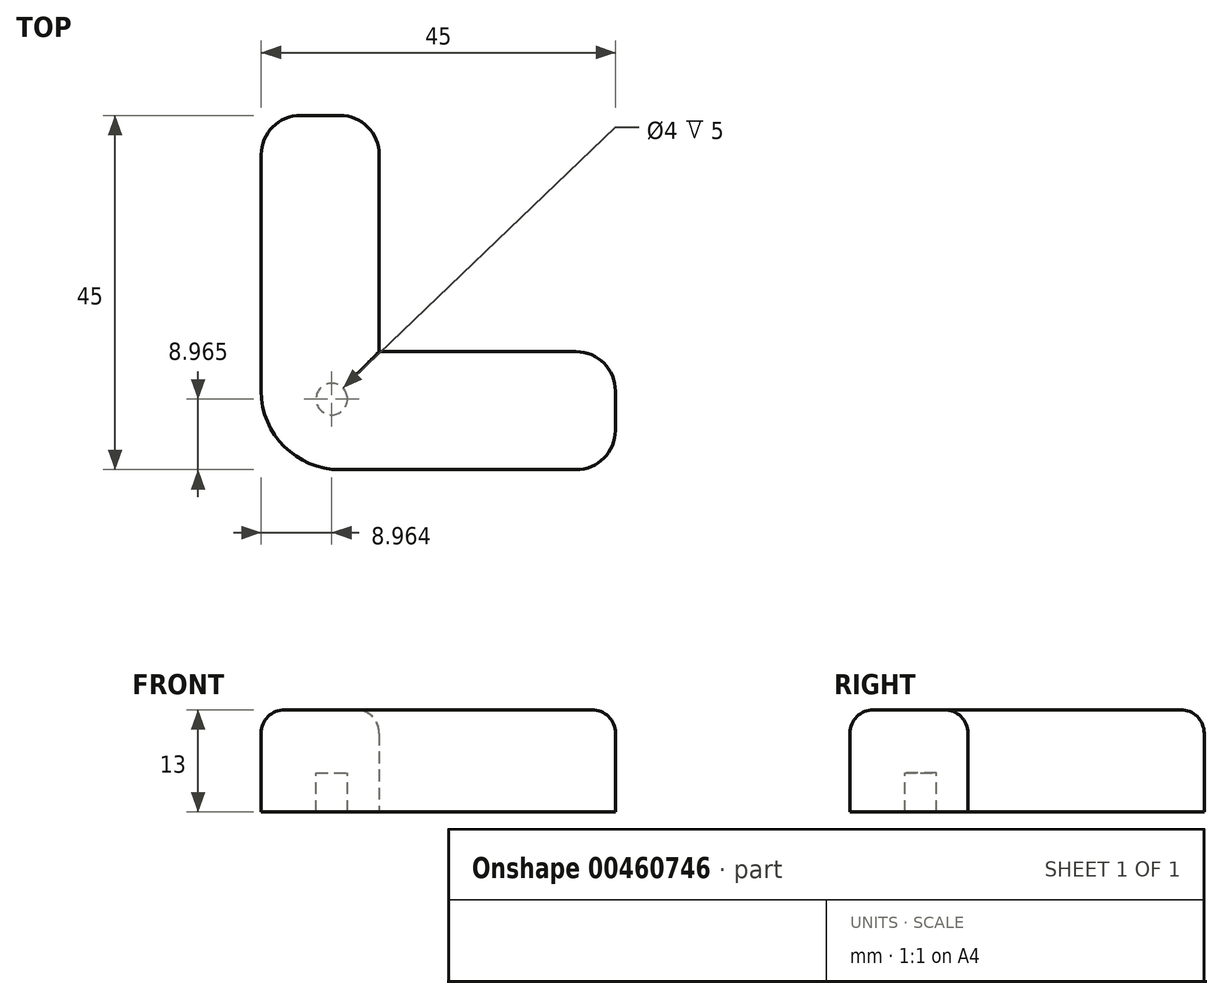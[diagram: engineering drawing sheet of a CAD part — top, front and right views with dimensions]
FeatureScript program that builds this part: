
annotation { "Feature Type Name" : "Feature", "Feature Type Description" : "" }
export const myFeature = defineFeature(function(context is Context, id is Id, definition is map)
    precondition{}
    {
        {
            var Q0;
            Q0=qCreatedBy(makeId("Top.planeOp"),FACE);
            var sketch = newSketch(context, id + "F0", { "sketchPlane" : qUnion([Q0])});
            skLineSegment(sketch, "E0", {"start": v(0, -5) * mm, "end": v(0, -35) * mm});
            skLineSegment(sketch, "E1", {"start": v(10, -45) * mm, "end": v(40, -45) * mm});
            skLineSegment(sketch, "E2", {"start": v(45, -40) * mm, "end": v(45, -35) * mm});
            skLineSegment(sketch, "E3", {"start": v(40, -30) * mm, "end": v(15, -30) * mm});
            skLineSegment(sketch, "E4", {"start": v(15, -30) * mm, "end": v(15, -5) * mm});
            skLineSegment(sketch, "E5", {"start": v(10, 0) * mm, "end": v(5, 0) * mm});
            skPoint(sketch, "E6.visualSharp", {"position": v(0, 0) * mm});
            skArc(sketch, "E6.filletArc", {"start": v(5, 0) * mm, "mid": v(1.46, -1.46) * mm, "end": v(0, -5) * mm});
            skPoint(sketch, "E7.visualSharp", {"position": v(15, 0) * mm});
            skArc(sketch, "E7.filletArc", {"start": v(15, -5) * mm, "mid": v(13.54, -1.46) * mm, "end": v(10, 0) * mm});
            skPoint(sketch, "E8.visualSharp", {"position": v(0, -45) * mm});
            skArc(sketch, "E8.filletArc", {"start": v(0, -35) * mm, "mid": v(2.93, -42.07) * mm, "end": v(10, -45) * mm});
            skPoint(sketch, "E9.visualSharp", {"position": v(45, -45) * mm});
            skArc(sketch, "E9.filletArc", {"start": v(40, -45) * mm, "mid": v(43.54, -43.54) * mm, "end": v(45, -40) * mm});
            skPoint(sketch, "E10.visualSharp", {"position": v(45, -30) * mm});
            skArc(sketch, "E10.filletArc", {"start": v(45, -35) * mm, "mid": v(43.54, -31.46) * mm, "end": v(40, -30) * mm});
            skSolve(sketch);
        }
        {
            var Q0;
            Q0 = qSketchRegion(id + "F0", true);
            extrude(context, id + "F1", {"entities" : qUnion([Q0]), "depth" : 8 * mm});
        }
        {
            var Q0;
            Q0=makeQuery(id+"F1.opExtrude","CAP_EDGE",EDGE,{"disambiguationData":[OSD([sQuery(id+"F0.wireOp",EDGE,"E4")])],"isStart":false});
            var Q1;
            Q1=makeQuery(id+"F1.opExtrude","CAP_EDGE",EDGE,{"disambiguationData":[OSD([sQuery(id+"F0.wireOp",EDGE,"E3")])],"isStart":false});
            var Q2;
            Q2=makeQuery(id+"F1.opExtrude","CAP_EDGE",EDGE,{"disambiguationData":[OSD([sQuery(id+"F0.wireOp",EDGE,"E7.filletArc")])],"isStart":false});
            var Q3;
            Q3=makeQuery(id+"F1.opExtrude","CAP_EDGE",EDGE,{"disambiguationData":[OSD([sQuery(id+"F0.wireOp",EDGE,"E5")])],"isStart":false});
            var Q4;
            Q4=makeQuery(id+"F1.opExtrude","CAP_EDGE",EDGE,{"disambiguationData":[OSD([sQuery(id+"F0.wireOp",EDGE,"E6.filletArc")])],"isStart":false});
            var Q5;
            Q5=makeQuery(id+"F1.opExtrude","CAP_EDGE",EDGE,{"disambiguationData":[OSD([sQuery(id+"F0.wireOp",EDGE,"E0")])],"isStart":false});
            var Q6;
            Q6=makeQuery(id+"F1.opExtrude","CAP_EDGE",EDGE,{"disambiguationData":[OSD([sQuery(id+"F0.wireOp",EDGE,"E8.filletArc")])],"isStart":false});
            var Q7;
            Q7=makeQuery(id+"F1.opExtrude","CAP_EDGE",EDGE,{"disambiguationData":[OSD([sQuery(id+"F0.wireOp",EDGE,"E1")])],"isStart":false});
            var Q8;
            Q8=makeQuery(id+"F1.opExtrude","CAP_EDGE",EDGE,{"disambiguationData":[OSD([sQuery(id+"F0.wireOp",EDGE,"E9.filletArc")])],"isStart":false});
            var Q9;
            Q9=makeQuery(id+"F1.opExtrude","CAP_EDGE",EDGE,{"disambiguationData":[OSD([sQuery(id+"F0.wireOp",EDGE,"E2")])],"isStart":false});
            var Q10;
            Q10=makeQuery(id+"F1.opExtrude","CAP_EDGE",EDGE,{"disambiguationData":[OSD([sQuery(id+"F0.wireOp",EDGE,"E10.filletArc")])],"isStart":false});
            fillet(context, id + "F2", {"entities" : qUnion([Q0, Q1, Q2, Q3, Q4, Q5, Q6, Q7, Q8, Q9, Q10]), "radius" : 3 * mm, "tangentPropagation" : true, "allowEdgeOverflow" : false});
        }
        {
            var Q0;
            Q0=makeQuery(id+"F1.opExtrude","CAP_FACE",FACE,{"disambiguationData":[OSD([sQuery(id+"F0.wireOp",EDGE,"E0"),sQuery(id+"F0.wireOp",EDGE,"E1"),sQuery(id+"F0.wireOp",EDGE,"E2"),sQuery(id+"F0.wireOp",EDGE,"E3"),sQuery(id+"F0.wireOp",EDGE,"E4"),sQuery(id+"F0.wireOp",EDGE,"E5"),sQuery(id+"F0.wireOp",EDGE,"E6.filletArc"),sQuery(id+"F0.wireOp",EDGE,"E7.filletArc"),sQuery(id+"F0.wireOp",EDGE,"E8.filletArc"),sQuery(id+"F0.wireOp",EDGE,"E9.filletArc"),sQuery(id+"F0.wireOp",EDGE,"E10.filletArc")])],"isStart":true});
            var sketch = newSketch(context, id + "F3", { "sketchPlane" : qUnion([Q0])});
            skLineSegment(sketch, "E11", {"start": v(15, 30) * mm, "end": v(2.93, 42.07) * mm});
            skCircle(sketch, "E12", {"center": v(8.96, 36.04) * mm, "radius": 2 * mm});
            skSolve(sketch);
        }
        {
            var Q0;
            {var subQ0=sQuery(id+"F3.wireOp",EDGE,"E12");var subQ1=sQuery(id+"F3.wireOp",EDGE,"E11");var subQ2=makeQuery(id+"F3.imprint","INTERSECT",VERTEX,{"disambiguationData":[OD(0.0)],"derivedFrom":[subQ1,subQ0]});Q0=makeQuery(id+"F3.imprint","IMPRINT",FACE,{"disambiguationData":[TD([[makeQuery(id+"F3.imprint","IMPRINT",EDGE,{"disambiguationData":[TD([[subQ2,-1.0]])],"derivedFrom":subQ1}),1.0]])]});}
            var Q1;
            {var subQ0=sQuery(id+"F3.wireOp",EDGE,"E12");var subQ1=sQuery(id+"F3.wireOp",EDGE,"E11");var subQ2=makeQuery(id+"F3.imprint","INTERSECT",VERTEX,{"disambiguationData":[OD(0.0)],"derivedFrom":[subQ1,subQ0]});Q1=makeQuery(id+"F3.imprint","IMPRINT",FACE,{"disambiguationData":[TD([[makeQuery(id+"F3.imprint","IMPRINT",EDGE,{"disambiguationData":[TD([[subQ2,-1.0]])],"derivedFrom":subQ1}),-1.0]])]});}
            extrude(context, id + "F4", {"entities" : qUnion([Q0, Q1]), "operationType" : NewBodyOperationType.ADD, "depth" : 5 * mm});
        }
    });
